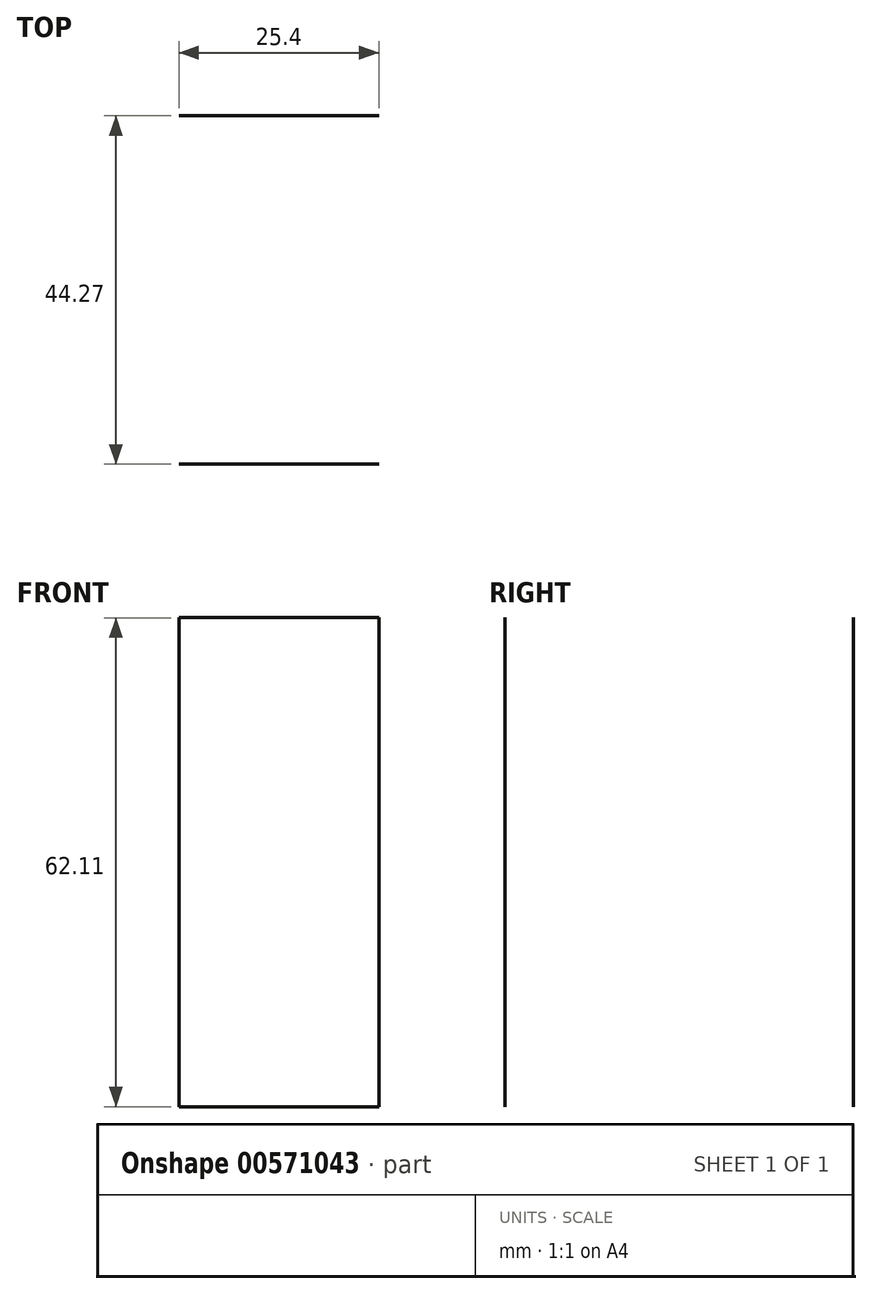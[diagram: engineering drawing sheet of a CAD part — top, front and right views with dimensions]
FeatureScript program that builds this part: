
annotation { "Feature Type Name" : "Feature", "Feature Type Description" : "" }
export const myFeature = defineFeature(function(context is Context, id is Id, definition is map)
    precondition{}
    {
        {
            var Q0;
            Q0=qCreatedBy(makeId("Right.planeOp"),FACE);
            var sketch = newSketch(context, id + "F0", { "sketchPlane" : qUnion([Q0])});
            skLineSegment(sketch, "E0.bottom", {"start": v(53, -86.8) * mm, "end": v(97.28, -86.8) * mm});
            skLineSegment(sketch, "E0.top", {"start": v(53, -24.7) * mm, "end": v(97.28, -24.7) * mm});
            skLineSegment(sketch, "E0.left", {"start": v(53, -86.8) * mm, "end": v(53, -24.7) * mm});
            skLineSegment(sketch, "E0.right", {"start": v(97.28, -86.8) * mm, "end": v(97.28, -24.7) * mm});
            skSolve(sketch);
        }
        {
            var Q0;
            Q0=sQuery(id+"F0.wireOp",EDGE,"E0.left");
            var Q1;
            Q1=sQuery(id+"F0.wireOp",EDGE,"E0.right");
            extrude(context, id + "F1", {"bodyType" : ToolBodyType.SURFACE, "surfaceEntities" : qUnion([Q0, Q1]), "depth" : 25.4 * mm, "offsetDistance" : 25.4 * mm});
        }
    });
